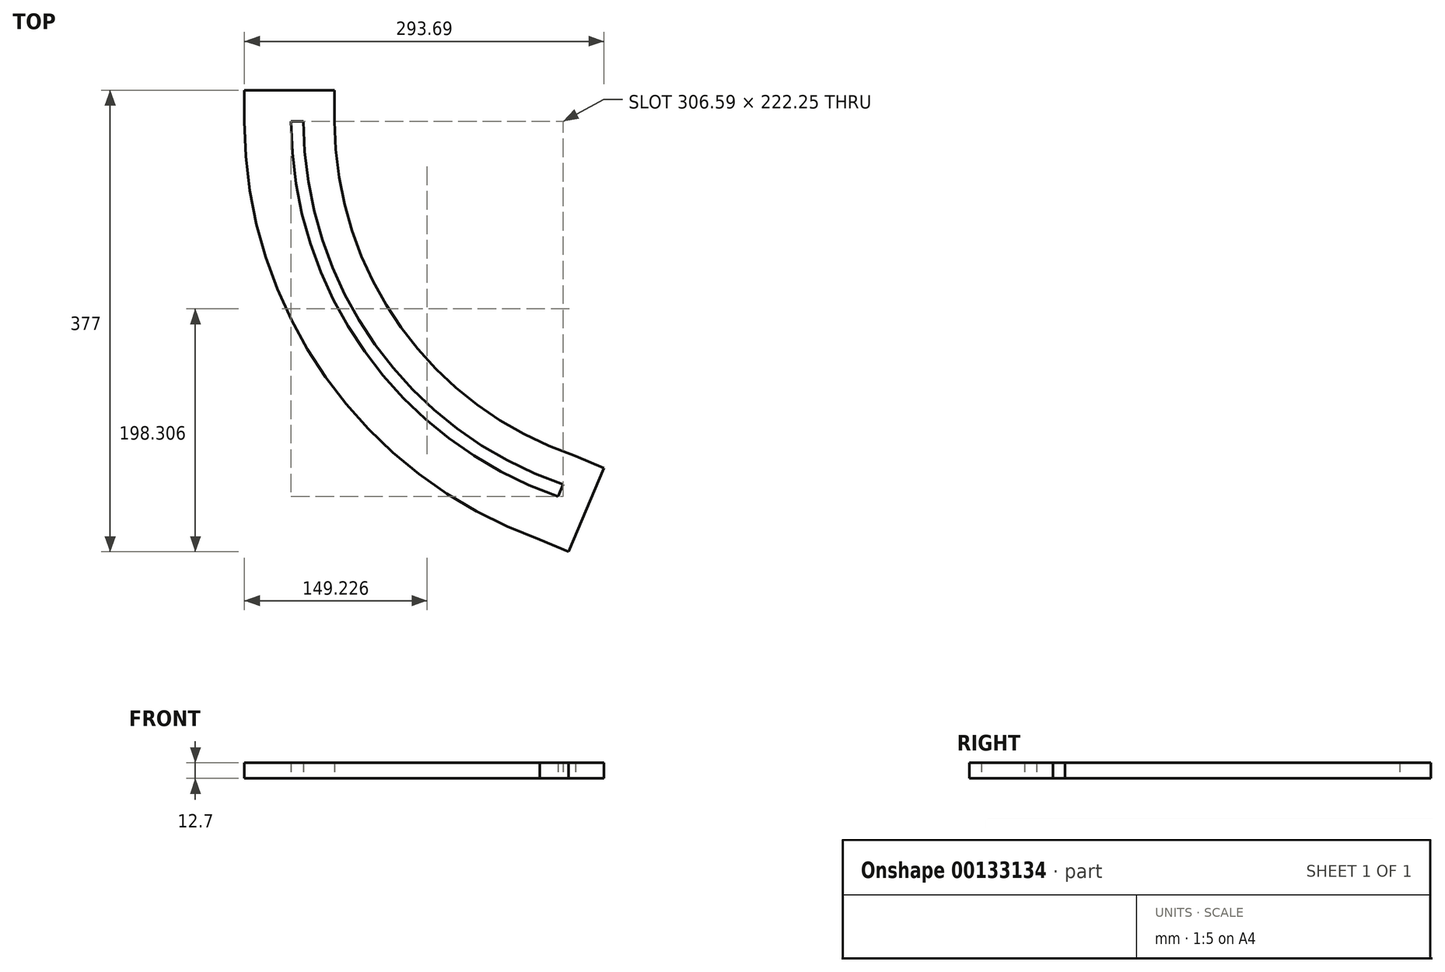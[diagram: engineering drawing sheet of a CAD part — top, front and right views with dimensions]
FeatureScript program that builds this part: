
annotation { "Feature Type Name" : "Feature", "Feature Type Description" : "" }
export const myFeature = defineFeature(function(context is Context, id is Id, definition is map)
    precondition{}
    {
        {
            var Q0;
            Q0=qCreatedBy(makeId("Top.planeOp"),FACE);
            var sketch = newSketch(context, id + "F0", { "sketchPlane" : qUnion([Q0])});
            skArc(sketch, "E0", {"start": v(-92.65, 157.88) * mm, "mid": v(-34.18, -24.5) * mm, "end": v(119.44, -138.9) * mm});
            skArc(sketch, "E1", {"start": v(-67.25, 157.88) * mm, "mid": v(-12.97, -10.53) * mm, "end": v(129.42, -115.55) * mm});
            skArc(sketch, "E2", {"start": v(-102.8, 157.88) * mm, "mid": v(-42.73, -30.23) * mm, "end": v(115.25, -148.7) * mm});
            skLineSegment(sketch, "E3", {"start": v(129.42, -115.55) * mm, "end": v(152.78, -125.53) * mm});
            skLineSegment(sketch, "E4", {"start": v(-140.9, 157.88) * mm, "end": v(-140.9, 183.28) * mm});
            skLineSegment(sketch, "E5", {"start": v(-67.25, 157.88) * mm, "end": v(-67.25, 183.28) * mm});
            skLineSegment(sketch, "E6", {"start": v(-140.9, 183.28) * mm, "end": v(-67.25, 183.28) * mm});
            skLineSegment(sketch, "E7", {"start": v(-102.8, 157.88) * mm, "end": v(-92.65, 157.88) * mm});
            skLineSegment(sketch, "E8", {"start": v(100.28, -183.74) * mm, "end": v(123.64, -193.72) * mm});
            skLineSegment(sketch, "E9", {"start": v(123.64, -193.72) * mm, "end": v(152.78, -125.53) * mm});
            skArc(sketch, "E10", {"start": v(-140.9, 157.88) * mm, "mid": v(-74.54, -51.21) * mm, "end": v(100.28, -183.74) * mm});
            skLineSegment(sketch, "E11", {"start": v(115.25, -148.7) * mm, "end": v(119.44, -138.9) * mm});
            skSolve(sketch);
        }
        {
            var Q0;
            Q0=makeQuery(id+"F0.imprint","IMPRINT",FACE,{"disambiguationData":[TD([[makeQuery(id+"F0.imprint","IMPRINT",EDGE,{"derivedFrom":sQuery(id+"F0.wireOp",EDGE,"E0")}),1.0]])]});
            extrude(context, id + "F1", {"entities" : qUnion([Q0]), "depth" : 12.7 * mm});
        }
    });
